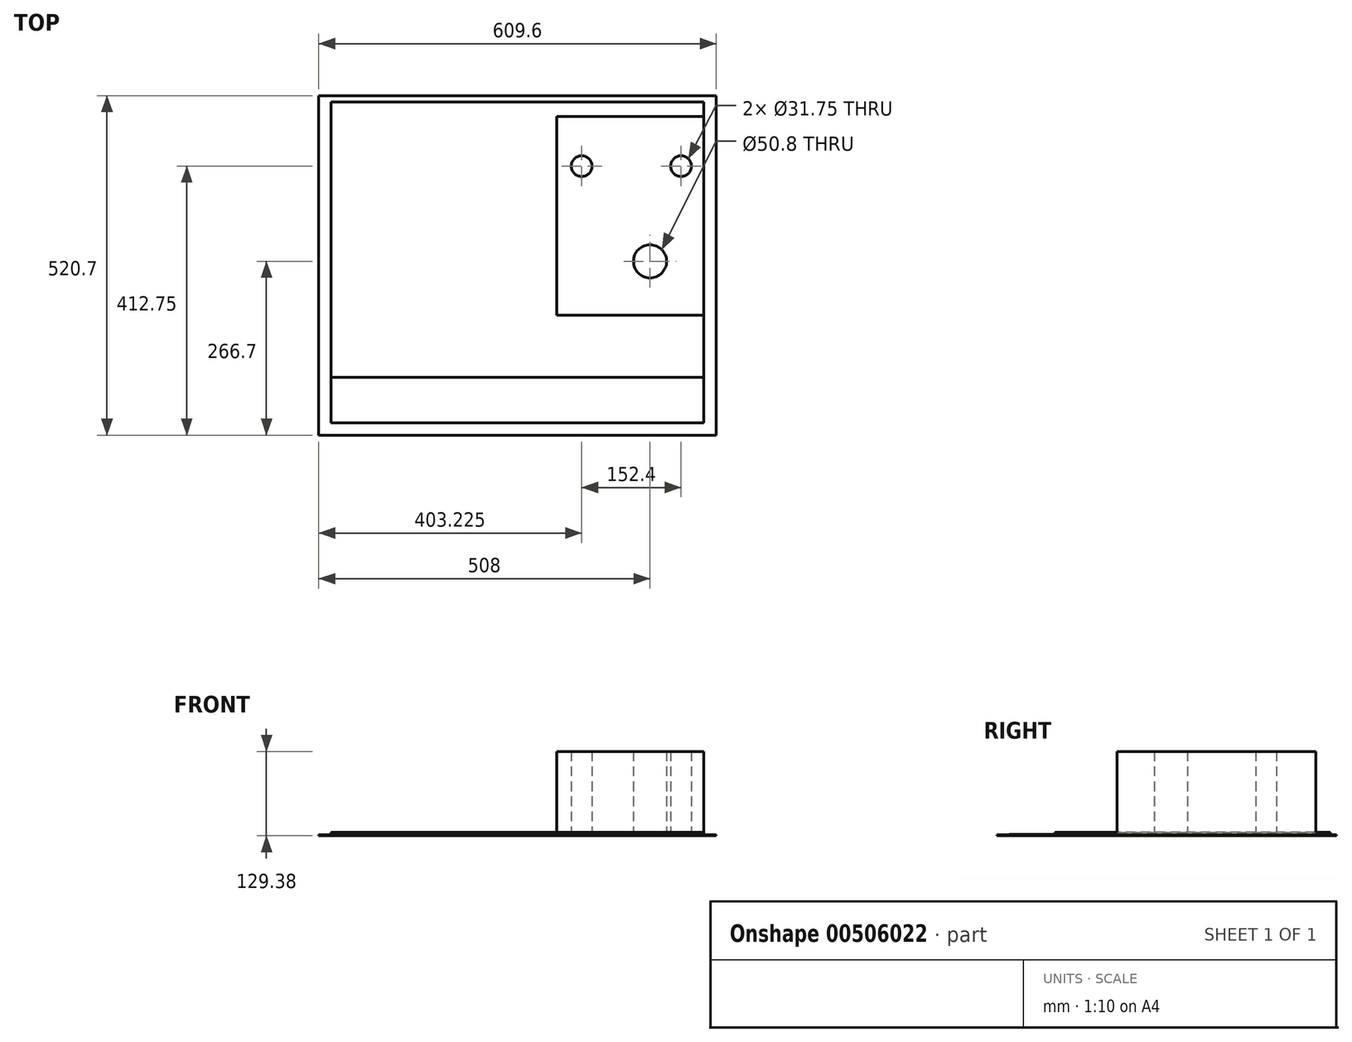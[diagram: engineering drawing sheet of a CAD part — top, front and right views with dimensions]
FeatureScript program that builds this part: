
annotation { "Feature Type Name" : "Feature", "Feature Type Description" : "" }
export const myFeature = defineFeature(function(context is Context, id is Id, definition is map)
    precondition{}
    {
        {
            var Q0;
            Q0=qCreatedBy(makeId("Top.planeOp"),FACE);
            var sketch = newSketch(context, id + "F0", { "sketchPlane" : qUnion([Q0])});
            skLineSegment(sketch, "E0.bottom", {"start": v(0, 0) * mm, "end": v(609.6, 0) * mm});
            skLineSegment(sketch, "E0.top", {"start": v(0, 520.7) * mm, "end": v(609.6, 520.7) * mm});
            skLineSegment(sketch, "E0.left", {"start": v(0, 0) * mm, "end": v(0, 520.7) * mm});
            skLineSegment(sketch, "E0.right", {"start": v(609.6, 0) * mm, "end": v(609.6, 520.7) * mm});
            skCircle(sketch, "E1", {"center": v(403.22, 412.75) * mm, "radius": 15.88 * mm});
            skCircle(sketch, "E2", {"center": v(555.62, 412.75) * mm, "radius": 15.88 * mm});
            skCircle(sketch, "E3", {"center": v(508, 266.7) * mm, "radius": 25.4 * mm});
            skSolve(sketch);
        }
        {
            var Q0;
            Q0=makeQuery(id+"F0.imprint","IMPRINT",FACE,{"disambiguationData":[TD([[makeQuery(id+"F0.imprint","IMPRINT",EDGE,{"derivedFrom":sQuery(id+"F0.wireOp",EDGE,"E0.bottom")}),1.0]])]});
            extrude(context, id + "F1", {"entities" : qUnion([Q0]), "depth" : 1.58 * mm, "offsetDistance" : 25.4 * mm});
        }
        {
            var Q0;
            Q0=makeQuery(id+"F1.opExtrude","CAP_FACE",FACE,{"disambiguationData":[OSD([sQuery(id+"F0.wireOp",EDGE,"E0.bottom"),sQuery(id+"F0.wireOp",EDGE,"E0.top"),sQuery(id+"F0.wireOp",EDGE,"E0.left"),sQuery(id+"F0.wireOp",EDGE,"E0.right"),sQuery(id+"F0.wireOp",EDGE,"E1"),sQuery(id+"F0.wireOp",EDGE,"E2"),sQuery(id+"F0.wireOp",EDGE,"E3")])],"isStart":false});
            var sketch = newSketch(context, id + "F2", { "sketchPlane" : qUnion([Q0])});
            skLineSegment(sketch, "E4.bottom", {"start": v(19.05, 511.18) * mm, "end": v(590.55, 511.18) * mm});
            skLineSegment(sketch, "E4.top", {"start": v(19.05, 19.05) * mm, "end": v(590.55, 19.05) * mm});
            skLineSegment(sketch, "E4.left", {"start": v(19.05, 511.18) * mm, "end": v(19.05, 19.05) * mm});
            skLineSegment(sketch, "E4.right", {"start": v(590.55, 511.18) * mm, "end": v(590.55, 19.05) * mm});
            skSolve(sketch);
        }
        {
            var Q0;
            Q0=makeQuery(id+"F2.imprint","IMPRINT",FACE,{"disambiguationData":[TD([[makeQuery(id+"F2.imprint","IMPRINT",EDGE,{"derivedFrom":sQuery(id+"F2.wireOp",EDGE,"E4.bottom")}),-1.0]])]});
            extrude(context, id + "F3", {"entities" : qUnion([Q0]), "operationType" : NewBodyOperationType.ADD, "depth" : 0.8 * mm, "offsetDistance" : 25.4 * mm});
        }
        {
            var Q0;
            Q0=makeQuery(id+"F3.opExtrude","CAP_FACE",FACE,{"disambiguationData":[OSD([sQuery(id+"F0.wireOp",EDGE,"E1"),sQuery(id+"F0.wireOp",EDGE,"E2"),sQuery(id+"F0.wireOp",EDGE,"E3"),sQuery(id+"F2.wireOp",EDGE,"E4.bottom"),sQuery(id+"F2.wireOp",EDGE,"E4.top"),sQuery(id+"F2.wireOp",EDGE,"E4.left"),sQuery(id+"F2.wireOp",EDGE,"E4.right")])],"isStart":false});
            var sketch = newSketch(context, id + "F4", { "sketchPlane" : qUnion([Q0])});
            skLineSegment(sketch, "E5.bottom", {"start": v(0, 88.9) * mm, "end": v(609.6, 88.9) * mm});
            skLineSegment(sketch, "E5.top", {"start": v(0, 0) * mm, "end": v(609.6, 0) * mm});
            skLineSegment(sketch, "E5.left", {"start": v(0, 88.9) * mm, "end": v(0, 0) * mm});
            skLineSegment(sketch, "E5.right", {"start": v(609.6, 88.9) * mm, "end": v(609.6, 0) * mm});
            skSolve(sketch);
        }
        {
            var Q0;
            {var subQ0=makeQuery(id+"F3.opExtrude","CAP_EDGE",EDGE,{"disambiguationData":[OSD([sQuery(id+"F2.wireOp",EDGE,"E4.bottom")])],"isStart":false});Q0=makeQuery(id+"F4.imprint","IMPRINT",FACE,{"disambiguationData":[TD([[makeQuery(id+"F4.imprint","IMPRINT",EDGE,{"derivedFrom":subQ0}),-1.0]])]});}
            extrude(context, id + "F5", {"entities" : qUnion([Q0]), "operationType" : NewBodyOperationType.ADD, "depth" : 3.17 * mm, "offsetDistance" : 25.4 * mm});
        }
        {
            var Q0;
            {var subQ0=makeQuery(id+"F3.opExtrude","CAP_EDGE",EDGE,{"disambiguationData":[OSD([sQuery(id+"F2.wireOp",EDGE,"E4.bottom")])],"isStart":false});Q0=makeQuery(id+"F4.imprint","IMPRINT",FACE,{"disambiguationData":[TD([[makeQuery(id+"F4.imprint","IMPRINT",EDGE,{"derivedFrom":subQ0}),-1.0]])]});}
            var sketch = newSketch(context, id + "F6", { "sketchPlane" : qUnion([Q0])});
            skLineSegment(sketch, "E6.bottom", {"start": v(365.12, 488.95) * mm, "end": v(596.9, 488.95) * mm});
            skLineSegment(sketch, "E6.top", {"start": v(365.12, 184.15) * mm, "end": v(596.9, 184.15) * mm});
            skLineSegment(sketch, "E6.left", {"start": v(365.12, 488.95) * mm, "end": v(365.12, 184.15) * mm});
            skLineSegment(sketch, "E6.right", {"start": v(596.9, 488.95) * mm, "end": v(596.9, 184.15) * mm});
            skSolve(sketch);
        }
        {
            var Q0;
            {var subQ0=sQuery(id+"F6.wireOp",EDGE,"E6.left");Q0=makeQuery(id+"F6.imprint","IMPRINT",FACE,{"disambiguationData":[TD([[makeQuery(id+"F6.imprint","IMPRINT",EDGE,{"derivedFrom":subQ0}),1.0]])]});}
            var Q1;
            Q1=sQuery(id+"F6.wireOp",EDGE,"E6.left");
            var Q2;
            Q2=sQuery(id+"F6.wireOp",EDGE,"E6.bottom");
            var Q3;
            Q3=sQuery(id+"F6.wireOp",EDGE,"E6.right");
            var Q4;
            Q4=sQuery(id+"F6.wireOp",EDGE,"E6.top");
            extrude(context, id + "F7", {"entities" : qUnion([Q0]), "operationType" : NewBodyOperationType.ADD, "surfaceEntities" : qUnion([Q1, Q2, Q3, Q4]), "depth" : 127 * mm, "offsetDistance" : 25.4 * mm});
        }
    });
